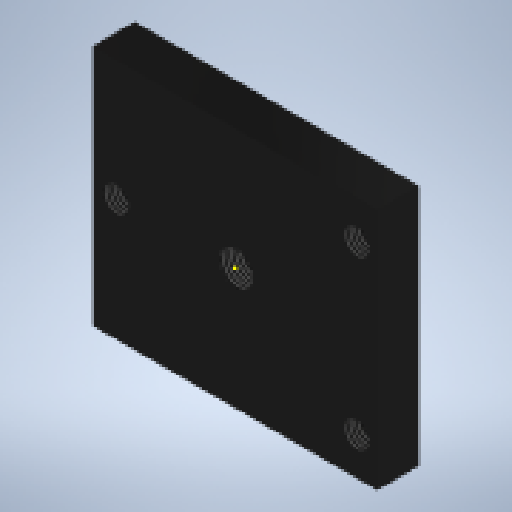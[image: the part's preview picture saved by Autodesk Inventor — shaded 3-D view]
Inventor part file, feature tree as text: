
AUTODESK INVENTOR PART (.ipt)
format: ipt  version: 2025.1 (Build 291241000, 241)  size: 146,944 bytes
history: native  units: in
note: dims shown in document units (in); Inventor stores cm internally (conversion verified against a paired STEP export)
features: sketch x4, other x3
ambient origin geometry x8: Origin, YZ Plane, XZ Plane, XY Plane, X Axis, Y Axis, Z Axis, Center Point
bodies: Solid1 (feature_tree)
feature tree (7):
  other  "Part2.ipt"
  other  "Solid1::Part2.ipt"
  other  "TaggingFeature1"
  sketch  "Sketch1"  dims[d0=0.3937in]
  sketch  "Sketch2"
  sketch  "Sketch3"
  sketch  "Sketch4"
